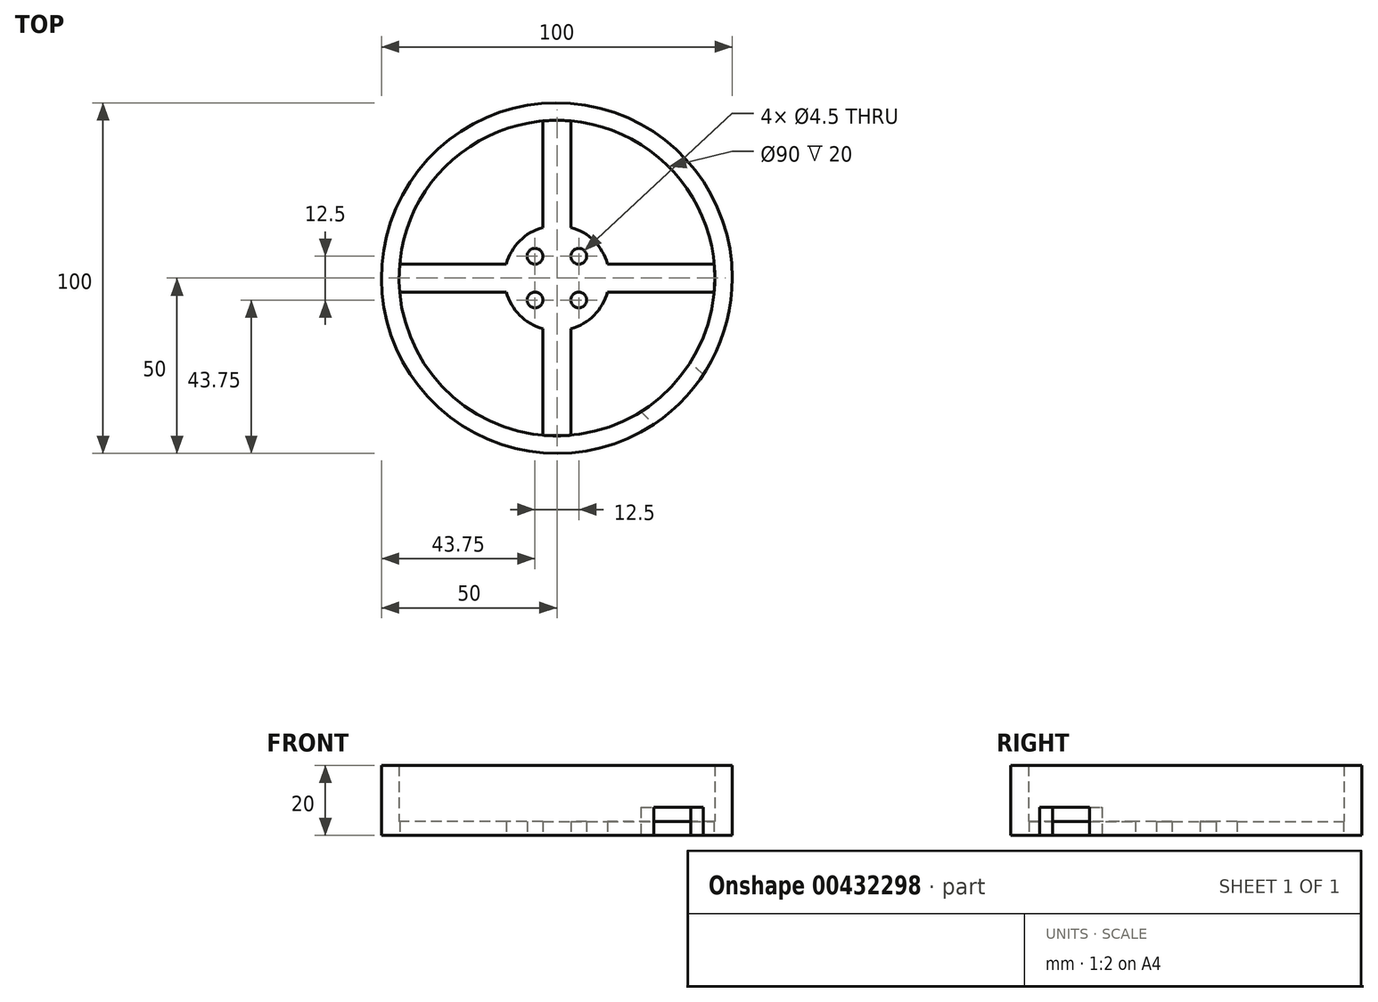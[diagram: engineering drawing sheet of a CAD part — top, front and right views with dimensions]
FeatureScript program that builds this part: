
annotation { "Feature Type Name" : "Feature", "Feature Type Description" : "" }
export const myFeature = defineFeature(function(context is Context, id is Id, definition is map)
    precondition{}
    {
        {
            var Q0;
            Q0=qCreatedBy(makeId("Top.planeOp"),FACE);
            var sketch = newSketch(context, id + "F0", { "sketchPlane" : qUnion([Q0])});
            skCircle(sketch, "E0", {"center": v(0, 0) * mm, "radius": 50 * mm});
            skCircle(sketch, "E1", {"center": v(0, 0) * mm, "radius": 45 * mm});
            skLineSegment(sketch, "E2", {"start": v(-4, 44.82) * mm, "end": v(-4, -44.82) * mm});
            skLineSegment(sketch, "E3", {"start": v(4, -44.82) * mm, "end": v(4, 44.82) * mm});
            skLineSegment(sketch, "E4", {"start": v(44.82, 4) * mm, "end": v(-44.82, 4) * mm});
            skLineSegment(sketch, "E5", {"start": v(-44.82, -4) * mm, "end": v(44.82, -4) * mm});
            skCircle(sketch, "E6", {"center": v(0, 0) * mm, "radius": 15 * mm});
            skCircle(sketch, "E7", {"center": v(6.25, 6.25) * mm, "radius": 2.25 * mm});
            skCircle(sketch, "E8.1.0", {"center": v(-6.25, 6.25) * mm, "radius": 2.25 * mm});
            skCircle(sketch, "E8.2.0", {"center": v(-6.25, -6.25) * mm, "radius": 2.25 * mm});
            skCircle(sketch, "E8.3.0", {"center": v(6.25, -6.25) * mm, "radius": 2.25 * mm});
            skLineSegment(sketch, "E9", {"start": v(0, 0) * mm, "end": v(35.36, -35.36) * mm});
            skLineSegment(sketch, "E10", {"start": v(41.71, -27.57) * mm, "end": v(30.93, -16.79) * mm});
            skLineSegment(sketch, "E11", {"start": v(16.79, -30.93) * mm, "end": v(27.57, -41.71) * mm});
            skSolve(sketch);
        }
        {
            var Q0;
            Q0=makeQuery(id+"F0.imprint","IMPRINT",FACE,{"disambiguationData":[TD([[makeQuery(id+"F0.imprint","IMPRINT",EDGE,{"derivedFrom":sQuery(id+"F0.wireOp",EDGE,"E0")}),1.0]])]});
            var Q1;
            {var subQ3=sQuery(id+"F0.wireOp",EDGE,"E10");var subQ15=sQuery(id+"F0.wireOp",EDGE,"E0");var subQ16=makeQuery(id+"F0.imprint","INTERSECT",VERTEX,{"derivedFrom":[subQ15,subQ3]});Q1=makeQuery(id+"F0.imprint","IMPRINT",FACE,{"disambiguationData":[TD([[makeQuery(id+"F0.imprint","IMPRINT",EDGE,{"disambiguationData":[TD([[subQ16,-1.0]])],"derivedFrom":subQ15}),1.0]])]});}
            extrude(context, id + "F1", {"entities" : qUnion([Q0, Q1]), "depth" : 20 * mm});
        }
        {
            var Q0;
            {var subQ0=sQuery(id+"F0.wireOp",EDGE,"E2");var subQ1=sQuery(id+"F0.wireOp",EDGE,"E1");var subQ2=makeQuery(id+"F0.imprint","INTERSECT",VERTEX,{"disambiguationData":[OD(0.0)],"derivedFrom":[subQ1,subQ0]});Q0=makeQuery(id+"F0.imprint","IMPRINT",FACE,{"disambiguationData":[TD([[makeQuery(id+"F0.imprint","IMPRINT",EDGE,{"disambiguationData":[TD([[subQ2,1.0]])],"derivedFrom":subQ1}),1.0]])]});}
            var Q1;
            {var subQ2=sQuery(id+"F0.wireOp",EDGE,"E6");var subQ4=sQuery(id+"F0.wireOp",EDGE,"E2");var subQ5=makeQuery(id+"F0.imprint","INTERSECT",VERTEX,{"disambiguationData":[OD(0.0)],"derivedFrom":[subQ4,subQ2]});Q1=makeQuery(id+"F0.imprint","IMPRINT",FACE,{"disambiguationData":[TD([[makeQuery(id+"F0.imprint","IMPRINT",EDGE,{"disambiguationData":[TD([[subQ5,-1.0]])],"derivedFrom":subQ4}),1.0]])]});}
            var Q2;
            {var subQ0=sQuery(id+"F0.wireOp",EDGE,"E4");var subQ1=sQuery(id+"F0.wireOp",EDGE,"E1");var subQ2=makeQuery(id+"F0.imprint","INTERSECT",VERTEX,{"disambiguationData":[OD(0.0)],"derivedFrom":[subQ1,subQ0]});Q2=makeQuery(id+"F0.imprint","IMPRINT",FACE,{"disambiguationData":[TD([[makeQuery(id+"F0.imprint","IMPRINT",EDGE,{"disambiguationData":[TD([[subQ2,1.0]])],"derivedFrom":subQ1}),1.0]])]});}
            var Q3;
            {var subQ0=sQuery(id+"F0.wireOp",EDGE,"E7");var subQ1=sQuery(id+"F0.wireOp",EDGE,"E3");var subQ2=makeQuery(id+"F0.imprint","INTERSECT",VERTEX,{"derivedFrom":[subQ1,subQ0]});Q3=makeQuery(id+"F0.imprint","IMPRINT",FACE,{"disambiguationData":[TD([[makeQuery(id+"F0.imprint","IMPRINT",EDGE,{"disambiguationData":[TD([[subQ2,-1.0]])],"derivedFrom":subQ1}),-1.0]])]});}
            var Q4;
            {var subQ1=sQuery(id+"F0.wireOp",EDGE,"E3");var subQ4=sQuery(id+"F0.wireOp",EDGE,"E5");var subQ5=makeQuery(id+"F0.imprint","INTERSECT",VERTEX,{"derivedFrom":[subQ1,subQ4]});Q4=makeQuery(id+"F0.imprint","IMPRINT",FACE,{"disambiguationData":[TD([[makeQuery(id+"F0.imprint","IMPRINT",EDGE,{"disambiguationData":[TD([[subQ5,-1.0]])],"derivedFrom":subQ1}),-1.0]])]});}
            var Q5;
            {var subQ0=sQuery(id+"F0.wireOp",EDGE,"E4");var subQ1=sQuery(id+"F0.wireOp",EDGE,"E3");var subQ2=makeQuery(id+"F0.imprint","INTERSECT",VERTEX,{"derivedFrom":[subQ1,subQ0]});Q5=makeQuery(id+"F0.imprint","IMPRINT",FACE,{"disambiguationData":[TD([[makeQuery(id+"F0.imprint","IMPRINT",EDGE,{"disambiguationData":[TD([[subQ2,-1.0]])],"derivedFrom":subQ1}),-1.0]])]});}
            var Q6;
            {var subQ0=sQuery(id+"F0.wireOp",EDGE,"E4");var subQ1=sQuery(id+"F0.wireOp",EDGE,"E2");var subQ2=makeQuery(id+"F0.imprint","INTERSECT",VERTEX,{"derivedFrom":[subQ1,subQ0]});Q6=makeQuery(id+"F0.imprint","IMPRINT",FACE,{"disambiguationData":[TD([[makeQuery(id+"F0.imprint","IMPRINT",EDGE,{"disambiguationData":[TD([[subQ2,-1.0]])],"derivedFrom":subQ1}),1.0]])]});}
            var Q7;
            {var subQ4=sQuery(id+"F0.wireOp",EDGE,"E4");var subQ7=sQuery(id+"F0.wireOp",EDGE,"E2");var subQ8=makeQuery(id+"F0.imprint","INTERSECT",VERTEX,{"derivedFrom":[subQ7,subQ4]});Q7=makeQuery(id+"F0.imprint","IMPRINT",FACE,{"disambiguationData":[TD([[makeQuery(id+"F0.imprint","IMPRINT",EDGE,{"disambiguationData":[TD([[subQ8,-1.0]])],"derivedFrom":subQ7}),-1.0]])]});}
            var Q8;
            {var subQ0=sQuery(id+"F0.wireOp",EDGE,"E6");var subQ1=sQuery(id+"F0.wireOp",EDGE,"E2");var subQ2=makeQuery(id+"F0.imprint","INTERSECT",VERTEX,{"disambiguationData":[OD(0.0)],"derivedFrom":[subQ1,subQ0]});Q8=makeQuery(id+"F0.imprint","IMPRINT",FACE,{"disambiguationData":[TD([[makeQuery(id+"F0.imprint","IMPRINT",EDGE,{"disambiguationData":[TD([[subQ2,-1.0]])],"derivedFrom":subQ1}),-1.0]])]});}
            var Q9;
            {var subQ0=sQuery(id+"F0.wireOp",EDGE,"E8.2.0");var subQ1=sQuery(id+"F0.wireOp",EDGE,"E2");var subQ2=makeQuery(id+"F0.imprint","INTERSECT",VERTEX,{"derivedFrom":[subQ1,subQ0]});Q9=makeQuery(id+"F0.imprint","IMPRINT",FACE,{"disambiguationData":[TD([[makeQuery(id+"F0.imprint","IMPRINT",EDGE,{"disambiguationData":[TD([[subQ2,-1.0]])],"derivedFrom":subQ1}),-1.0]])]});}
            var Q10;
            {var subQ0=sQuery(id+"F0.wireOp",EDGE,"E8.3.0");var subQ1=sQuery(id+"F0.wireOp",EDGE,"E3");var subQ2=makeQuery(id+"F0.imprint","INTERSECT",VERTEX,{"derivedFrom":[subQ1,subQ0]});Q10=makeQuery(id+"F0.imprint","IMPRINT",FACE,{"disambiguationData":[TD([[makeQuery(id+"F0.imprint","IMPRINT",EDGE,{"disambiguationData":[TD([[subQ2,-1.0]])],"derivedFrom":subQ1}),-1.0]])]});}
            var Q11;
            {var subQ0=sQuery(id+"F0.wireOp",EDGE,"E6");var subQ1=sQuery(id+"F0.wireOp",EDGE,"E3");var subQ2=makeQuery(id+"F0.imprint","INTERSECT",VERTEX,{"disambiguationData":[OD(0.0)],"derivedFrom":[subQ1,subQ0]});Q11=makeQuery(id+"F0.imprint","IMPRINT",FACE,{"disambiguationData":[TD([[makeQuery(id+"F0.imprint","IMPRINT",EDGE,{"disambiguationData":[TD([[subQ2,-1.0]])],"derivedFrom":subQ1}),-1.0]])]});}
            var Q12;
            {var subQ0=sQuery(id+"F0.wireOp",EDGE,"E2");var subQ1=sQuery(id+"F0.wireOp",EDGE,"E1");var subQ2=makeQuery(id+"F0.imprint","INTERSECT",VERTEX,{"disambiguationData":[OD(1.0)],"derivedFrom":[subQ1,subQ0]});Q12=makeQuery(id+"F0.imprint","IMPRINT",FACE,{"disambiguationData":[TD([[makeQuery(id+"F0.imprint","IMPRINT",EDGE,{"disambiguationData":[TD([[subQ2,-1.0]])],"derivedFrom":subQ1}),1.0]])]});}
            var Q13;
            {var subQ0=sQuery(id+"F0.wireOp",EDGE,"E4");var subQ1=sQuery(id+"F0.wireOp",EDGE,"E1");var subQ2=makeQuery(id+"F0.imprint","INTERSECT",VERTEX,{"disambiguationData":[OD(1.0)],"derivedFrom":[subQ1,subQ0]});Q13=makeQuery(id+"F0.imprint","IMPRINT",FACE,{"disambiguationData":[TD([[makeQuery(id+"F0.imprint","IMPRINT",EDGE,{"disambiguationData":[TD([[subQ2,-1.0]])],"derivedFrom":subQ1}),1.0]])]});}
            var Q14;
            {var subQ4=sQuery(id+"F0.wireOp",EDGE,"E2");var subQ7=sQuery(id+"F0.wireOp",EDGE,"E5");var subQ9=makeQuery(id+"F0.imprint","INTERSECT",VERTEX,{"derivedFrom":[subQ4,subQ7]});Q14=makeQuery(id+"F0.imprint","IMPRINT",FACE,{"disambiguationData":[TD([[makeQuery(id+"F0.imprint","IMPRINT",EDGE,{"disambiguationData":[TD([[subQ9,-1.0]])],"derivedFrom":subQ4}),1.0]])]});}
            var Q15;
            {var subQ0=sQuery(id+"F0.wireOp",EDGE,"E5");var subQ1=sQuery(id+"F0.wireOp",EDGE,"E2");var subQ2=makeQuery(id+"F0.imprint","INTERSECT",VERTEX,{"derivedFrom":[subQ1,subQ0]});Q15=makeQuery(id+"F0.imprint","IMPRINT",FACE,{"disambiguationData":[TD([[makeQuery(id+"F0.imprint","IMPRINT",EDGE,{"disambiguationData":[TD([[subQ2,-1.0]])],"derivedFrom":subQ1}),-1.0]])]});}
            var Q16;
            {var subQ0=sQuery(id+"F0.wireOp",EDGE,"E8.1.0");var subQ1=sQuery(id+"F0.wireOp",EDGE,"E2");var subQ2=makeQuery(id+"F0.imprint","INTERSECT",VERTEX,{"derivedFrom":[subQ1,subQ0]});Q16=makeQuery(id+"F0.imprint","IMPRINT",FACE,{"disambiguationData":[TD([[makeQuery(id+"F0.imprint","IMPRINT",EDGE,{"disambiguationData":[TD([[subQ2,-1.0]])],"derivedFrom":subQ1}),-1.0]])]});}
            var Q17;
            {var subQ0=sQuery(id+"F0.wireOp",EDGE,"E8.3.0");var subQ1=sQuery(id+"F0.wireOp",EDGE,"E5");var subQ2=makeQuery(id+"F0.imprint","INTERSECT",VERTEX,{"derivedFrom":[subQ1,subQ0]});Q17=makeQuery(id+"F0.imprint","IMPRINT",FACE,{"disambiguationData":[TD([[makeQuery(id+"F0.imprint","IMPRINT",EDGE,{"disambiguationData":[TD([[subQ2,-1.0]])],"derivedFrom":subQ1}),-1.0]])]});}
            var Q18;
            {var subQ0=sQuery(id+"F0.wireOp",EDGE,"E8.3.0");var subQ1=sQuery(id+"F0.wireOp",EDGE,"E5");var subQ2=makeQuery(id+"F0.imprint","INTERSECT",VERTEX,{"derivedFrom":[subQ1,subQ0]});Q18=makeQuery(id+"F0.imprint","IMPRINT",FACE,{"disambiguationData":[TD([[makeQuery(id+"F0.imprint","IMPRINT",EDGE,{"disambiguationData":[TD([[subQ2,-1.0]])],"derivedFrom":subQ0}),-1.0]])]});}
            extrude(context, id + "F2", {"entities" : qUnion([Q0, Q1, Q2, Q3, Q4, Q5, Q6, Q7, Q8, Q9, Q10, Q11, Q12, Q13, Q14, Q15, Q16, Q17, Q18]), "operationType" : NewBodyOperationType.ADD, "depth" : 4 * mm});
        }
        {
            var Q0;
            {var subQ0=sQuery(id+"F0.wireOp",EDGE,"E9");var subQ1=sQuery(id+"F0.wireOp",EDGE,"E0");var subQ2=makeQuery(id+"F0.imprint","INTERSECT",VERTEX,{"derivedFrom":[subQ1,subQ0]});Q0=makeQuery(id+"F0.imprint","IMPRINT",FACE,{"disambiguationData":[TD([[makeQuery(id+"F0.imprint","IMPRINT",EDGE,{"disambiguationData":[TD([[subQ2,-1.0]])],"derivedFrom":subQ1}),1.0]])]});}
            var Q1;
            {var subQ0=sQuery(id+"F0.wireOp",EDGE,"E9");var subQ1=sQuery(id+"F0.wireOp",EDGE,"E0");var subQ2=makeQuery(id+"F0.imprint","INTERSECT",VERTEX,{"derivedFrom":[subQ1,subQ0]});Q1=makeQuery(id+"F0.imprint","IMPRINT",FACE,{"disambiguationData":[TD([[makeQuery(id+"F0.imprint","IMPRINT",EDGE,{"disambiguationData":[TD([[subQ2,1.0]])],"derivedFrom":subQ1}),1.0]])]});}
            extrude(context, id + "F3", {"entities" : qUnion([Q0, Q1]), "operationType" : NewBodyOperationType.REMOVE, "depth" : 8 * mm});
        }
    });
